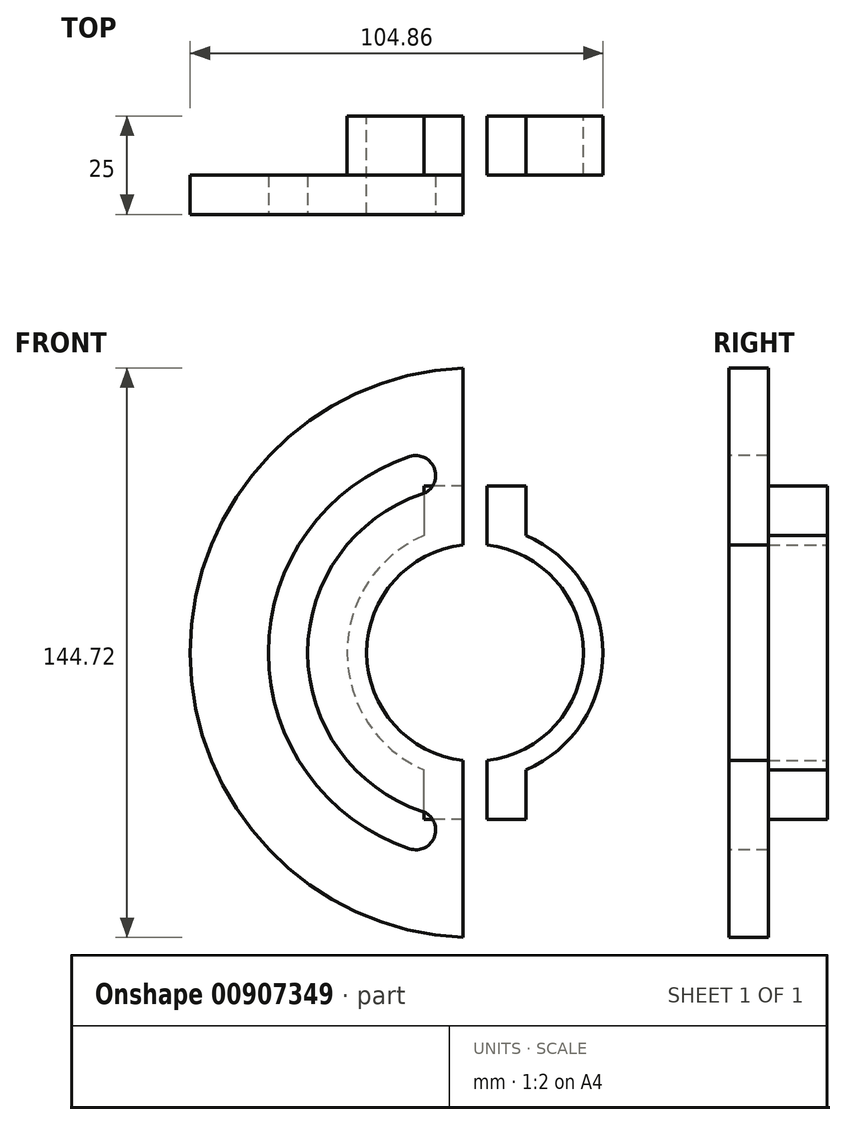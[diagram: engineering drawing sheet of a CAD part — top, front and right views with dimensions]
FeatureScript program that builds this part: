
annotation { "Feature Type Name" : "Feature", "Feature Type Description" : "" }
export const myFeature = defineFeature(function(context is Context, id is Id, definition is map)
    precondition{}
    {
        {
            var Q0;
            Q0=qCreatedBy(makeId("Front.planeOp"),FACE);
            var sketch = newSketch(context, id + "F0", { "sketchPlane" : qUnion([Q0])});
            skCircle(sketch, "E0", {"center": v(0, 0) * mm, "radius": 27.5 * mm, "construction": true});
            skLineSegment(sketch, "E1.left", {"start": v(-3, 50) * mm, "end": v(-3, -50) * mm, "construction": true});
            skPoint(sketch, "E2", {"position": v(-3, 27.34) * mm});
            skPoint(sketch, "E3", {"position": v(-3, -27.34) * mm});
            skPoint(sketch, "E4", {"position": v(-27.5, 0) * mm});
            skArc(sketch, "E5", {"start": v(-3, 27.34) * mm, "mid": v(-27.5, 0) * mm, "end": v(-3, -27.34) * mm});
            skArc(sketch, "E6.0", {"start": v(-13, 29.79) * mm, "mid": v(-32.5, 0) * mm, "end": v(-13, -29.79) * mm});
            skLineSegment(sketch, "E7", {"start": v(-3, 32.36) * mm, "end": v(-3, 42.36) * mm});
            skLineSegment(sketch, "E8", {"start": v(-3, 42.36) * mm, "end": v(-13, 42.36) * mm});
            skLineSegment(sketch, "E9", {"start": v(-13, 42.36) * mm, "end": v(-13, 29.79) * mm});
            skLineSegment(sketch, "E10", {"start": v(-3, -32.36) * mm, "end": v(-3, -42.36) * mm});
            skLineSegment(sketch, "E11", {"start": v(-3, -42.36) * mm, "end": v(-13, -42.36) * mm});
            skLineSegment(sketch, "E12", {"start": v(-13, -42.36) * mm, "end": v(-13, -29.79) * mm});
            skLineSegment(sketch, "E13", {"start": v(-3, 32.36) * mm, "end": v(-3, 27.34) * mm});
            skLineSegment(sketch, "E14", {"start": v(-3, -32.36) * mm, "end": v(-3, -27.34) * mm});
            skLineSegment(sketch, "E15.MirrorCS", {"start": v(3, 32.36) * mm, "end": v(3, 27.34) * mm});
            skLineSegment(sketch, "E16.MirrorCS", {"start": v(3, -32.36) * mm, "end": v(3, -27.34) * mm});
            skLineSegment(sketch, "E17.MirrorCS", {"start": v(3, 42.36) * mm, "end": v(13, 42.36) * mm});
            skLineSegment(sketch, "E18.MirrorCS", {"start": v(3, -42.36) * mm, "end": v(13, -42.36) * mm});
            skArc(sketch, "E19.MirrorCS", {"start": v(3, 27.34) * mm, "mid": v(27.5, 0) * mm, "end": v(3, -27.34) * mm});
            skArc(sketch, "E20.MirrorCS", {"start": v(13, 29.79) * mm, "mid": v(32.5, 0) * mm, "end": v(13, -29.79) * mm});
            skLineSegment(sketch, "E21.MirrorCS", {"start": v(13, 42.36) * mm, "end": v(13, 29.79) * mm});
            skLineSegment(sketch, "E22.MirrorCS", {"start": v(13, -42.36) * mm, "end": v(13, -29.79) * mm});
            skLineSegment(sketch, "E23.MirrorCS", {"start": v(3, -32.36) * mm, "end": v(3, -42.36) * mm});
            skLineSegment(sketch, "E24.MirrorCS", {"start": v(3, 32.36) * mm, "end": v(3, 42.36) * mm});
            skPoint(sketch, "E25.MirrorP", {"position": v(27.5, 0) * mm});
            skPoint(sketch, "E26.MirrorP", {"position": v(3, -27.34) * mm});
            skPoint(sketch, "E27.MirrorP", {"position": v(3, 27.34) * mm});
            skSolve(sketch);
        }
        {
            var Q0;
            Q0 = qSketchRegion(id + "F0", true);
            extrude(context, id + "F1", {"entities" : qUnion([Q0]), "depth" : 15 * mm, "offsetDistance" : 25 * mm});
        }
        {
            var Q0;
            Q0=makeQuery(id+"F1.opExtrude","CAP_FACE",FACE,{"disambiguationData":[OSD([sQuery(id+"F0.wireOp",EDGE,"E5"),sQuery(id+"F0.wireOp",EDGE,"E6.0"),sQuery(id+"F0.wireOp",EDGE,"E7"),sQuery(id+"F0.wireOp",EDGE,"E8"),sQuery(id+"F0.wireOp",EDGE,"E9"),sQuery(id+"F0.wireOp",EDGE,"E10"),sQuery(id+"F0.wireOp",EDGE,"E11"),sQuery(id+"F0.wireOp",EDGE,"E12"),sQuery(id+"F0.wireOp",EDGE,"E13"),sQuery(id+"F0.wireOp",EDGE,"E14")])],"isStart":false});
            var sketch = newSketch(context, id + "F2", { "sketchPlane" : qUnion([Q0])});
            skArc(sketch, "E28.0", {"start": v(-3, 27.34) * mm, "mid": v(-27.5, 0) * mm, "end": v(-3, -27.34) * mm});
            skLineSegment(sketch, "E29.0", {"start": v(-3, 42.36) * mm, "end": v(-3, 27.34) * mm});
            skLineSegment(sketch, "E30.0", {"start": v(-3, -27.34) * mm, "end": v(-3, -42.36) * mm});
            skLineSegment(sketch, "E31", {"start": v(-3, -42.36) * mm, "end": v(-3, -72.36) * mm});
            skLineSegment(sketch, "E32", {"start": v(-3, 42.36) * mm, "end": v(-3, 72.36) * mm});
            skPoint(sketch, "E33", {"position": v(-72.36, 0) * mm});
            skArc(sketch, "E34", {"start": v(-3, 72.36) * mm, "mid": v(-72.36, 0) * mm, "end": v(-3, -72.36) * mm});
            skSolve(sketch);
        }
        {
            var Q0;
            Q0 = qSketchRegion(id + "F2", true);
            extrude(context, id + "F3", {"entities" : qUnion([Q0]), "operationType" : NewBodyOperationType.ADD, "depth" : 10 * mm, "offsetDistance" : 25 * mm});
        }
        {
            var Q0;
            Q0=makeQuery(id+"F3.opExtrude","CAP_FACE",FACE,{"disambiguationData":[OSD([sQuery(id+"F2.wireOp",EDGE,"E28.0"),sQuery(id+"F2.wireOp",EDGE,"E29.0"),sQuery(id+"F2.wireOp",EDGE,"E30.0"),sQuery(id+"F2.wireOp",EDGE,"E31"),sQuery(id+"F2.wireOp",EDGE,"E32"),sQuery(id+"F2.wireOp",EDGE,"E34")])],"isStart":false});
            var sketch = newSketch(context, id + "F4", { "sketchPlane" : qUnion([Q0])});
            skArc(sketch, "E35.0", {"start": v(-3, 27.34) * mm, "mid": v(-27.5, 0) * mm, "end": v(-3, -27.34) * mm, "construction": true});
            skLineSegment(sketch, "E36.0", {"start": v(-3, 72.36) * mm, "end": v(-3, 27.34) * mm, "construction": true});
            skLineSegment(sketch, "E37.0", {"start": v(-3, -27.34) * mm, "end": v(-3, -72.36) * mm, "construction": true});
            skArc(sketch, "E38.0", {"start": v(-15, 45.07) * mm, "mid": v(-47.5, 0) * mm, "end": v(-15, -45.07) * mm});
            skArc(sketch, "E39.0.startCap", {"start": v(-16.58, 49.81) * mm, "mid": v(-10.26, 46.65) * mm, "end": v(-13.42, 40.33) * mm});
            skArc(sketch, "E39.0.endCap", {"start": v(-13.42, -40.33) * mm, "mid": v(-10.26, -46.65) * mm, "end": v(-16.58, -49.81) * mm});
            skArc(sketch, "E39.0.left", {"start": v(-13.42, 40.33) * mm, "mid": v(-42.5, 0) * mm, "end": v(-13.42, -40.33) * mm});
            skArc(sketch, "E39.0.right", {"start": v(-16.58, 49.81) * mm, "mid": v(-52.5, 0) * mm, "end": v(-16.58, -49.81) * mm});
            skSolve(sketch);
        }
        {
            var Q0;
            Q0 = qSketchRegion(id + "F4", true);
            extrude(context, id + "F5", {"entities" : qUnion([Q0]), "operationType" : NewBodyOperationType.REMOVE, "oppositeDirection" : true, "depth" : 10 * mm, "offsetDistance" : 25 * mm});
        }
    });
